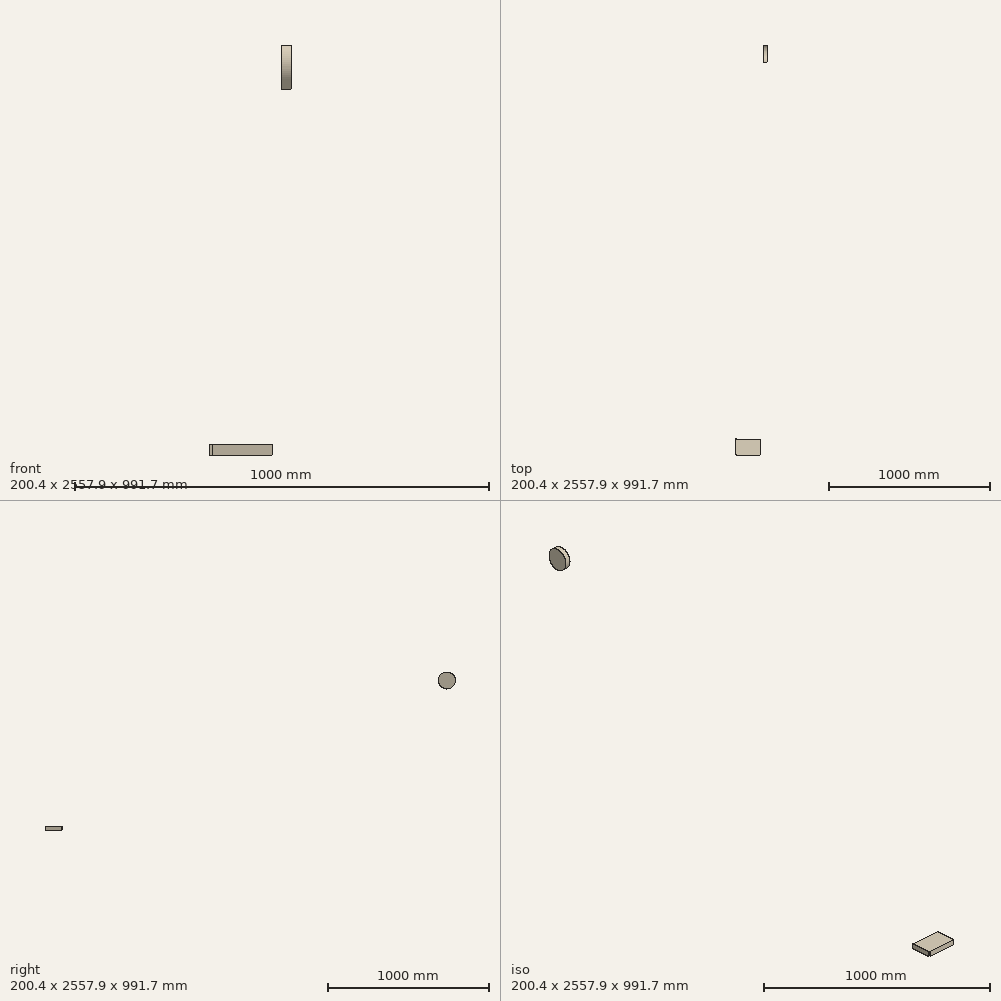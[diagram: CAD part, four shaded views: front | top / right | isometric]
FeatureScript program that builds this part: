
annotation { "Feature Type Name" : "Feature", "Feature Type Description" : "" }
export const myFeature = defineFeature(function(context is Context, id is Id, definition is map)
    precondition{}
    {
        {
            var Q0;
            Q0=qCreatedBy(makeId("Top.planeOp"),FACE);
            var sketch = newSketch(context, id + "F0", { "sketchPlane" : qUnion([Q0])});
            skLineSegment(sketch, "E0.bottom", {"start": v(-175.05, 19.59) * mm, "end": v(-165.98, 19.59) * mm});
            skLineSegment(sketch, "E0.top", {"start": v(-175.05, -77.55) * mm, "end": v(-165.98, -77.55) * mm});
            skLineSegment(sketch, "E0.left", {"start": v(-175.05, 19.59) * mm, "end": v(-175.05, -77.55) * mm});
            skLineSegment(sketch, "E0.right", {"start": v(-165.98, 19.59) * mm, "end": v(-165.98, -77.55) * mm});
            skLineSegment(sketch, "E1.bottom", {"start": v(-165.98, -85.28) * mm, "end": v(-21.25, -85.28) * mm});
            skLineSegment(sketch, "E1.top", {"start": v(-165.98, 16.46) * mm, "end": v(-21.25, 16.46) * mm});
            skLineSegment(sketch, "E1.left", {"start": v(-165.98, -85.28) * mm, "end": v(-165.98, 16.46) * mm});
            skLineSegment(sketch, "E1.right", {"start": v(-21.25, -85.28) * mm, "end": v(-21.25, 16.46) * mm});
            skSolve(sketch);
        }
        {
            var Q0;
            Q0 = qSketchRegion(id + "F0", true);
            extrude(context, id + "F1", {"entities" : qUnion([Q0]), "depth" : 25.4 * mm, "offsetDistance" : 25.4 * mm});
        }
        {
            var Q0;
            Q0=qCreatedBy(makeId("Right.planeOp"),FACE);
            var sketch = newSketch(context, id + "F2", { "sketchPlane" : qUnion([Q0])});
            skCircle(sketch, "E2", {"center": v(2419.67, 938.7) * mm, "radius": 52.99 * mm});
            skSolve(sketch);
        }
        {
            var Q0;
            Q0 = qSketchRegion(id + "F2", true);
            extrude(context, id + "F3", {"entities" : qUnion([Q0]), "depth" : 25.4 * mm, "offsetDistance" : 25.4 * mm});
        }
    });
